# Revit family: HMD
name_source: partatom
category: Mechanical Equipment
units: mm (PartAtom-declared; Revit-internal decimal feet)

## family parameters
Always vertical = Yes
Cut with Voids When Loaded = No
Part Type = Normal
Room Calculation Point = No
Round Connector Dimension = Use Diameter
Shared = No
Work Plane-Based = No

## types (3) — shared parameters
-(C_W/2) = -1' - 4 1/2"
0 = 0' - 0"
1.5 = 0' - 1 1/2"
2" = 0' - 2"
3/4 = 0' - 0 3/4"
4 = 0' - 4"
A = 2' - 10 1/2"
A/2 = 1' - 5 1/4"
B = 5' - 10"
C = 2' - 6 7/16"
C_H = 2' - 2 3/16"
C_W = 2' - 9"
C_W/2 = 1' - 4 1/2"
D-B = 2' - 7 1/2"
E = 0' - 4 7/8"
F = 1' - 2"
FILTER_H = 2' - 10 3/8"
FILTER_W = 2' - 1 3/4"
G = 0' - 3"
H = 0' - 4 7/8"
Manufacturer = Loren Cook Company
Model = HMD
ONE EIGTH = 0' - 0 1/8"
RO = 2' - 6"
RO/2 = 1' - 3"
RO2 = 5' - 5 1/2"
RO2/2 = 2' - 8 3/4"
T_SQ = 4' - 3 7/8"
T_SQ/2 = 2' - 1 15/16"
Type Comments = Heated Make-Up Direct
URL = www.lorencook.com
W = 1' - 10 1/2"

## type names (no varying parameters)
- HMD-2400
- HMD-3400
- HMD-4100

## geometry (parser evidence)
native form markers: Sweep x2
no freeform markers — native parametric forms only
